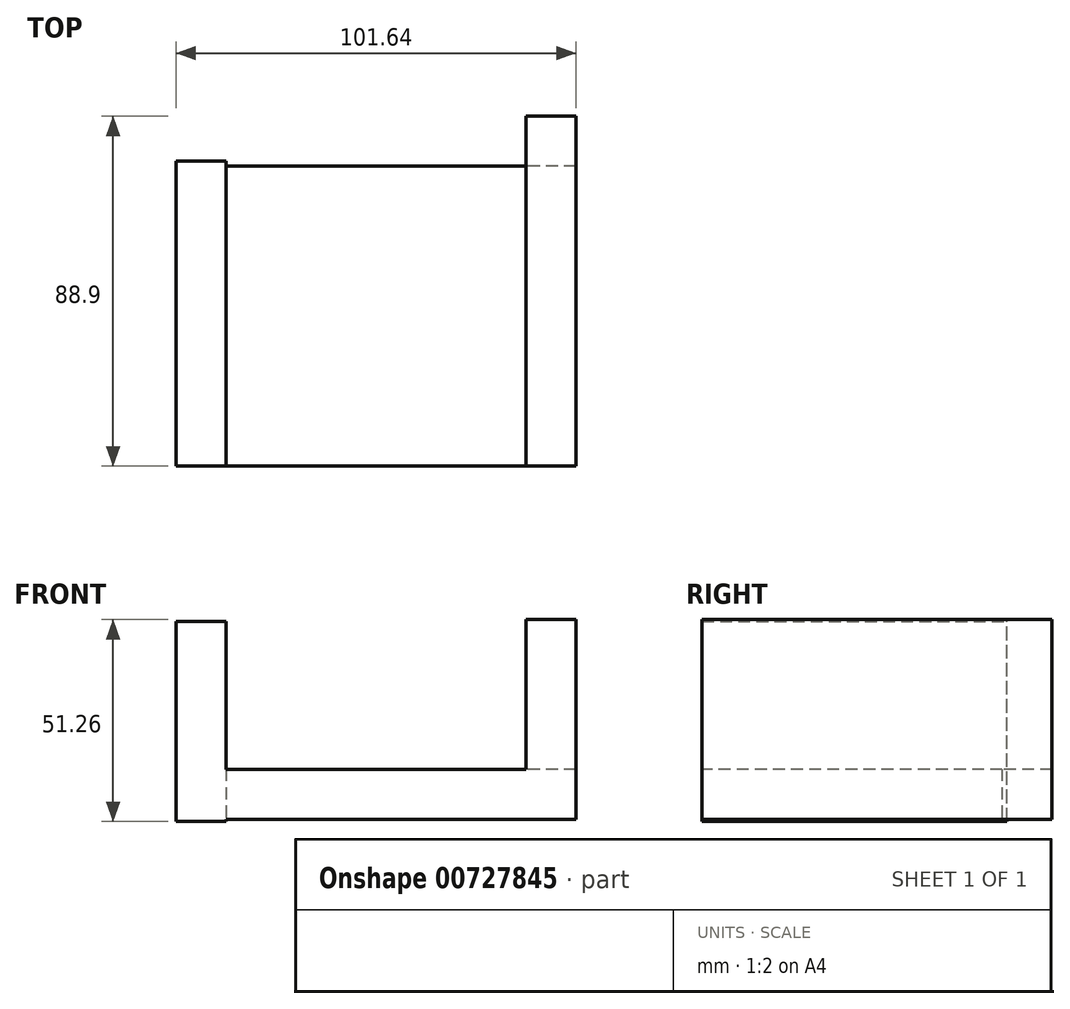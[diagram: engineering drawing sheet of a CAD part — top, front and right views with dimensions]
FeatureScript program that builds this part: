
annotation { "Feature Type Name" : "Feature", "Feature Type Description" : "" }
export const myFeature = defineFeature(function(context is Context, id is Id, definition is map)
    precondition{}
    {
        {
            var Q0;
            Q0=qCreatedBy(makeId("Right.planeOp"),FACE);
            var sketch = newSketch(context, id + "F0", { "sketchPlane" : qUnion([Q0])});
            skLineSegment(sketch, "E0.bottom", {"start": v(-31.75, 6.35) * mm, "end": v(31.75, 6.35) * mm});
            skLineSegment(sketch, "E0.top", {"start": v(-31.75, -6.35) * mm, "end": v(31.75, -6.35) * mm});
            skLineSegment(sketch, "E0.left", {"start": v(-31.75, 6.35) * mm, "end": v(-31.75, -6.35) * mm});
            skLineSegment(sketch, "E0.right", {"start": v(31.75, 6.35) * mm, "end": v(31.75, -6.35) * mm});
            skPoint(sketch, "E0.middle", {"position": v(0, 0) * mm});
            skSolve(sketch);
        }
        {
            var Q0;
            Q0 = qSketchRegion(id + "F0", true);
            extrude(context, id + "F1", {"entities" : qUnion([Q0]), "depth" : 88.9 * mm, "offsetDistance" : 25.4 * mm});
        }
        {
            var Q0;
            Q0=qCreatedBy(makeId("Front.planeOp"),FACE);
            var sketch = newSketch(context, id + "F2", { "sketchPlane" : qUnion([Q0])});
            skLineSegment(sketch, "E1.bottom", {"start": v(0, -6.86) * mm, "end": v(-12.7, -6.86) * mm});
            skLineSegment(sketch, "E1.top", {"start": v(0, 43.94) * mm, "end": v(-12.7, 43.94) * mm});
            skLineSegment(sketch, "E1.left", {"start": v(0, -6.86) * mm, "end": v(0, 43.94) * mm});
            skLineSegment(sketch, "E1.right", {"start": v(-12.7, -6.86) * mm, "end": v(-12.7, 43.94) * mm});
            skSolve(sketch);
        }
        {
            var Q0;
            Q0=makeQuery(id+"F2.imprint","IMPRINT",FACE,{"disambiguationData":[TD([[makeQuery(id+"F2.imprint","IMPRINT",EDGE,{"derivedFrom":sQuery(id+"F2.wireOp",EDGE,"E1.bottom")}),-1.0]])]});
            extrude(context, id + "F3", {"entities" : qUnion([Q0]), "operationType" : NewBodyOperationType.ADD, "depth" : 44.45 * mm, "offsetDistance" : 25.4 * mm});
        }
        {
            var Q0;
            Q0=makeQuery(id+"F1.opExtrude","SWEPT_FACE",FACE,{"disambiguationData":[OSD([sQuery(id+"F0.wireOp",EDGE,"E0.left")])]});
            extrude(context, id + "F4", {"entities" : qUnion([Q0]), "operationType" : NewBodyOperationType.ADD, "depth" : 12.7 * mm, "offsetDistance" : 25.4 * mm});
        }
        {
            var Q0;
            Q0=makeQuery(id+"F3.opExtrude","CAP_FACE",FACE,{"disambiguationData":[OSD([sQuery(id+"F2.wireOp",EDGE,"E1.bottom"),sQuery(id+"F2.wireOp",EDGE,"E1.top"),sQuery(id+"F2.wireOp",EDGE,"E1.left"),sQuery(id+"F2.wireOp",EDGE,"E1.right")])],"isStart":true});
            extrude(context, id + "F5", {"entities" : qUnion([Q0]), "operationType" : NewBodyOperationType.ADD, "depth" : 33.02 * mm, "offsetDistance" : 25.4 * mm});
        }
        {
            var Q0;
            Q0=qCreatedBy(makeId("Front.planeOp"),FACE);
            var sketch = newSketch(context, id + "F6", { "sketchPlane" : qUnion([Q0])});
            skLineSegment(sketch, "E2.bottom", {"start": v(76.24, -6.4) * mm, "end": v(88.94, -6.4) * mm});
            skLineSegment(sketch, "E2.top", {"start": v(76.24, 44.4) * mm, "end": v(88.94, 44.4) * mm});
            skLineSegment(sketch, "E2.left", {"start": v(76.24, -6.4) * mm, "end": v(76.24, 44.4) * mm});
            skLineSegment(sketch, "E2.right", {"start": v(88.94, -6.4) * mm, "end": v(88.94, 44.4) * mm});
            skSolve(sketch);
        }
        {
            var Q0;
            Q0=makeQuery(id+"F6.imprint","IMPRINT",FACE,{"disambiguationData":[TD([[makeQuery(id+"F6.imprint","IMPRINT",EDGE,{"derivedFrom":sQuery(id+"F6.wireOp",EDGE,"E2.bottom")}),1.0]])]});
            extrude(context, id + "F7", {"entities" : qUnion([Q0]), "operationType" : NewBodyOperationType.ADD, "depth" : 44.45 * mm, "offsetDistance" : 25.4 * mm});
        }
        {
            var Q0;
            Q0=makeQuery(id+"F7.opExtrude","CAP_FACE",FACE,{"disambiguationData":[OSD([sQuery(id+"F6.wireOp",EDGE,"E2.bottom"),sQuery(id+"F6.wireOp",EDGE,"E2.top"),sQuery(id+"F6.wireOp",EDGE,"E2.left"),sQuery(id+"F6.wireOp",EDGE,"E2.right")])],"isStart":true});
            extrude(context, id + "F8", {"entities" : qUnion([Q0]), "operationType" : NewBodyOperationType.ADD, "depth" : 44.45 * mm, "offsetDistance" : 25.4 * mm});
        }
    });
